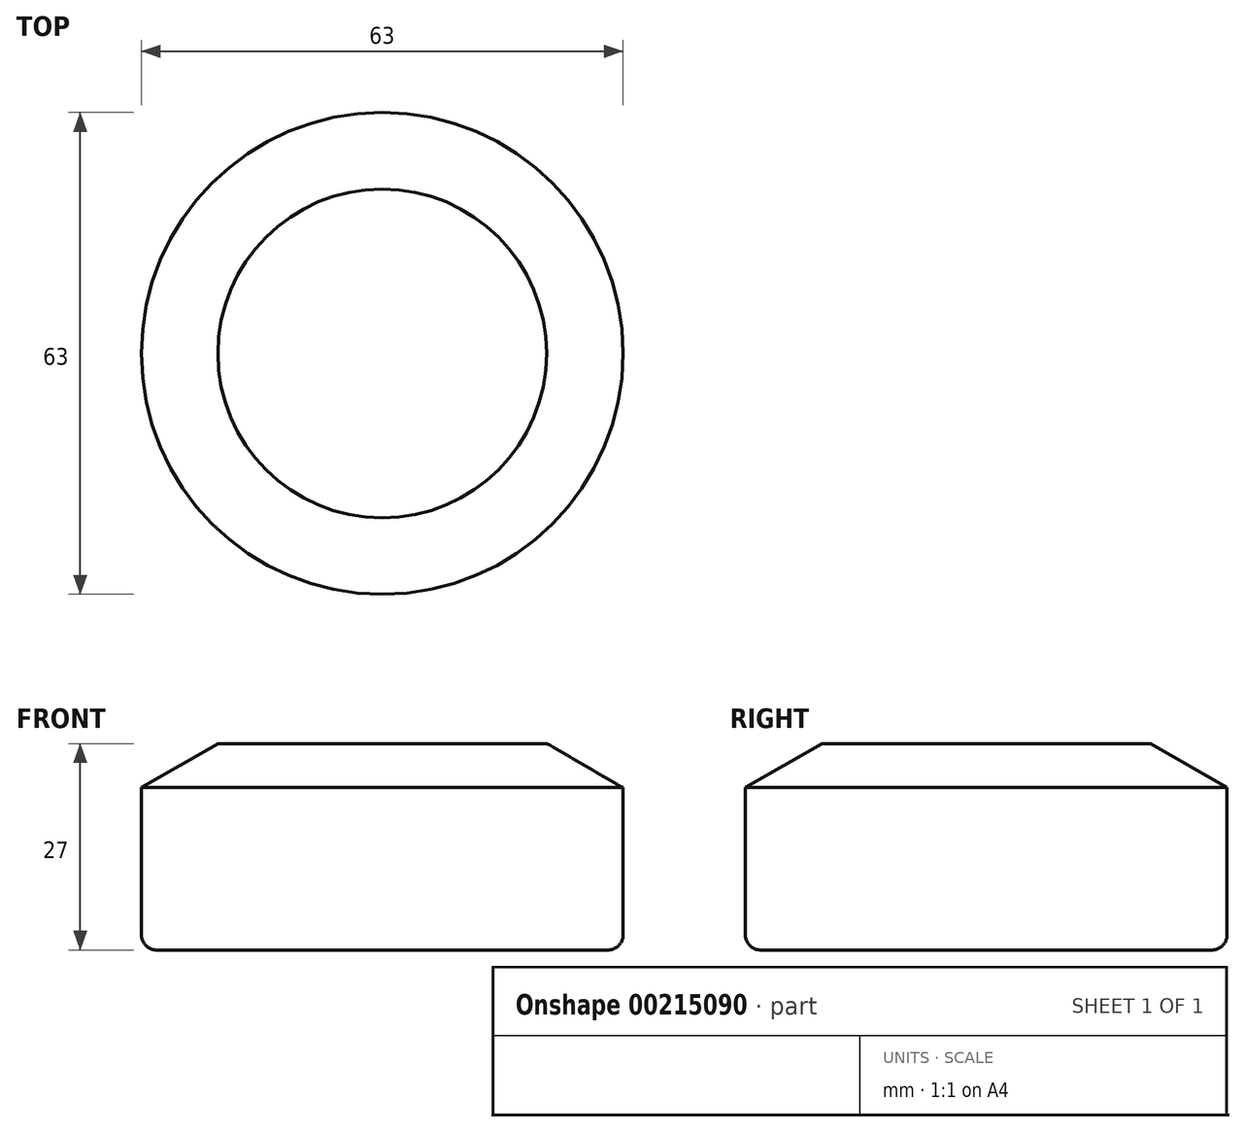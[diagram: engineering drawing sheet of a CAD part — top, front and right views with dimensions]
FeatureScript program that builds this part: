
annotation { "Feature Type Name" : "Feature", "Feature Type Description" : "" }
export const myFeature = defineFeature(function(context is Context, id is Id, definition is map)
    precondition{}
    {
        {
            var Q0;
            Q0=qCreatedBy(makeId("Top.planeOp"),FACE);
            var sketch = newSketch(context, id + "F0", { "sketchPlane" : qUnion([Q0])});
            skCircle(sketch, "E0", {"center": v(0, 0) * mm, "radius": 31.5 * mm});
            skSolve(sketch);
        }
        {
            var Q0;
            Q0=qSketchRegion(id+"F0",true);
            extrude(context, id + "F1", {"entities" : qUnion([Q0]), "depth" : 27 * mm});
        }
        {
            var Q0;
            Q0=makeQuery(id+"F1.opExtrude","CAP_EDGE",EDGE,{"disambiguationData":[OSD([sQuery(id+"F0.wireOp",EDGE,"E0")])],"isStart":false});
            chamfer(context, id + "F2", {"entities" : qUnion([Q0]), "chamferType" : ChamferType.OFFSET_ANGLE, "width" : 10 * mm, "oppositeDirection" : false, "angle" : 30 * degree, "tangentPropagation" : true});
        }
        {
            var Q0;
            Q0=makeQuery(id+"F1.opExtrude","CAP_EDGE",EDGE,{"disambiguationData":[OSD([sQuery(id+"F0.wireOp",EDGE,"E0")])],"isStart":true});
            fillet(context, id + "F3", {"entities" : qUnion([Q0]), "radius" : 2 * mm, "tangentPropagation" : true, "allowEdgeOverflow" : false});
        }
    });
